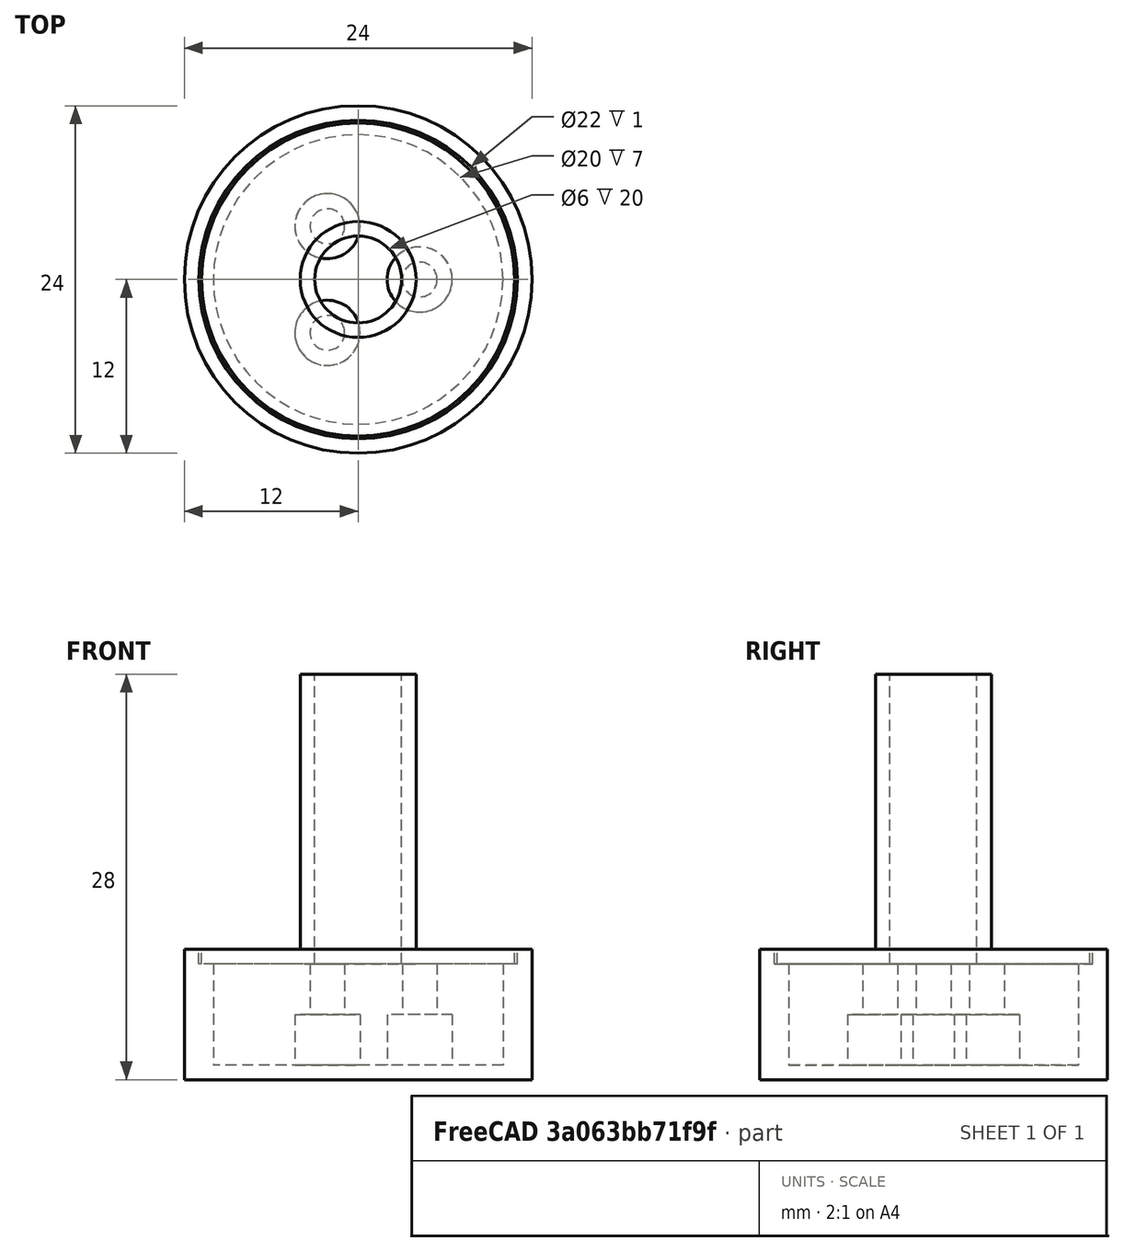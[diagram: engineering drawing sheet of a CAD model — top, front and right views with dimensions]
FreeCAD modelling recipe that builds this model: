
FCSTD DOCUMENT  (FreeCAD 0.17R13509 (Git))
Label: insert_bottom
License: All rights reserved
LicenseURL: http://en.wikipedia.org/wiki/All_rights_reserved
objects: Part::Cylinder×9, Part::Cut×4, Part::MultiFuse×2, Part::FeaturePython×1
note: 16 computed .brp shape members not serialized (recipe doc carries the construction recipe); baked Part::Feature solids carry a one-line shape summary decoded from their .brp

FEATURE [Part::Cylinder] Cylinder153  label="Body"
  Angle = 360
  AttacherType = Attacher::AttachEngine3D
  Height = 7
  Placement = pos=(0,0,1) rot=(0,0,1;0rad)
  Radius = 10
FEATURE [Part::Cylinder] Cylinder147  label="ThreadedSection"
  Angle = 360
  AttacherType = Attacher::AttachEngine3D
  Height = 1
  Placement = pos=(0,0,4.5) rot=(0,0,1;0rad)
  Radius = 1
FEATURE [Part::Cylinder] Cylinder156  label="BottomWireOutlet"
  Angle = 360
  AttacherType = Attacher::AttachEngine3D
  Height = 14
  Placement = pos=(0,0,-7) rot=(0,0,1;0rad)
  Radius = 1.2
FEATURE [Part::Cylinder] Cylinder157  label="SealSubtraction"
  Angle = 360
  AttacherType = Attacher::AttachEngine3D
  Height = 7
  Placement = pos=(0,0,4.5) rot=(0,0,1;0rad)
  Radius = 2.25
FEATURE [Part::MultiFuse] Fusion
  Placement = pos=(4.25,0,0) rot=(0,0,1;0rad)
  Shapes = -> [Cylinder147,Cylinder157,Cylinder156]
FEATURE [Part::FeaturePython] Array  label="SealArray"  # Draft array (typed FeaturePython)
  Angle = 360
  ArrayType = 1
  Axis = (0,0,1)
  Base = -> Fusion
  Center = (0,0,0)
  Fuse = false
  IntervalAxis = (0,0,0)
  IntervalX = (1,0,0)
  IntervalY = (0,1,0)
  IntervalZ = (0,0,0)
  NumberPolar = 3
  NumberX = 2
  NumberY = 2
  NumberZ = 1
FEATURE [Part::Cut] Cut
  Base = -> Cylinder153
  Placement = pos=(0,0,9) rot=(1,0,0;3.14159rad)
  Tool = -> Array
FEATURE [Part::Cylinder] Cylinder158  label="Cylinder001"
  Angle = 360
  AttacherType = Attacher::AttachEngine3D
  Height = 23
  Placement = pos=(0,0,8) rot=(0,0,1;0rad)
  Radius = 3
FEATURE [Part::Cylinder] Cylinder159  label="Reservoir"
  Angle = 360
  AttacherType = Attacher::AttachEngine3D
  Height = 20
  Placement = pos=(0,0,8) rot=(0,0,1;0rad)
  Radius = 4
FEATURE [Part::Cylinder] Cylinder
  Angle = 360
  AttacherType = Attacher::AttachEngine3D
  Height = 9
  Radius = 12
FEATURE [Part::Cylinder] Cylinder160  label="Cylinder003"
  Angle = 360
  AttacherType = Attacher::AttachEngine3D
  Height = 4
  Placement = pos=(0,0,8) rot=(0,0,1;0rad)
  Radius = 11
FEATURE [Part::Cut] Cut001
  Base = -> Cylinder
  Tool = -> Cylinder160
FEATURE [Part::Cylinder] Cylinder161  label="Lid"
  Angle = 360
  AttacherType = Attacher::AttachEngine3D
  Height = 1
  Placement = pos=(0,0,8) rot=(0,0,1;0rad)
  Radius = 10.8
FEATURE [Part::MultiFuse] Fusion001
  Shapes = -> [Cylinder159,Cylinder161]
FEATURE [Part::Cut] Cut002
  Base = -> Fusion001
  Tool = -> Cylinder158
FEATURE [Part::Cut] Cut003
  Base = -> Cut001
  Tool = -> Cut
